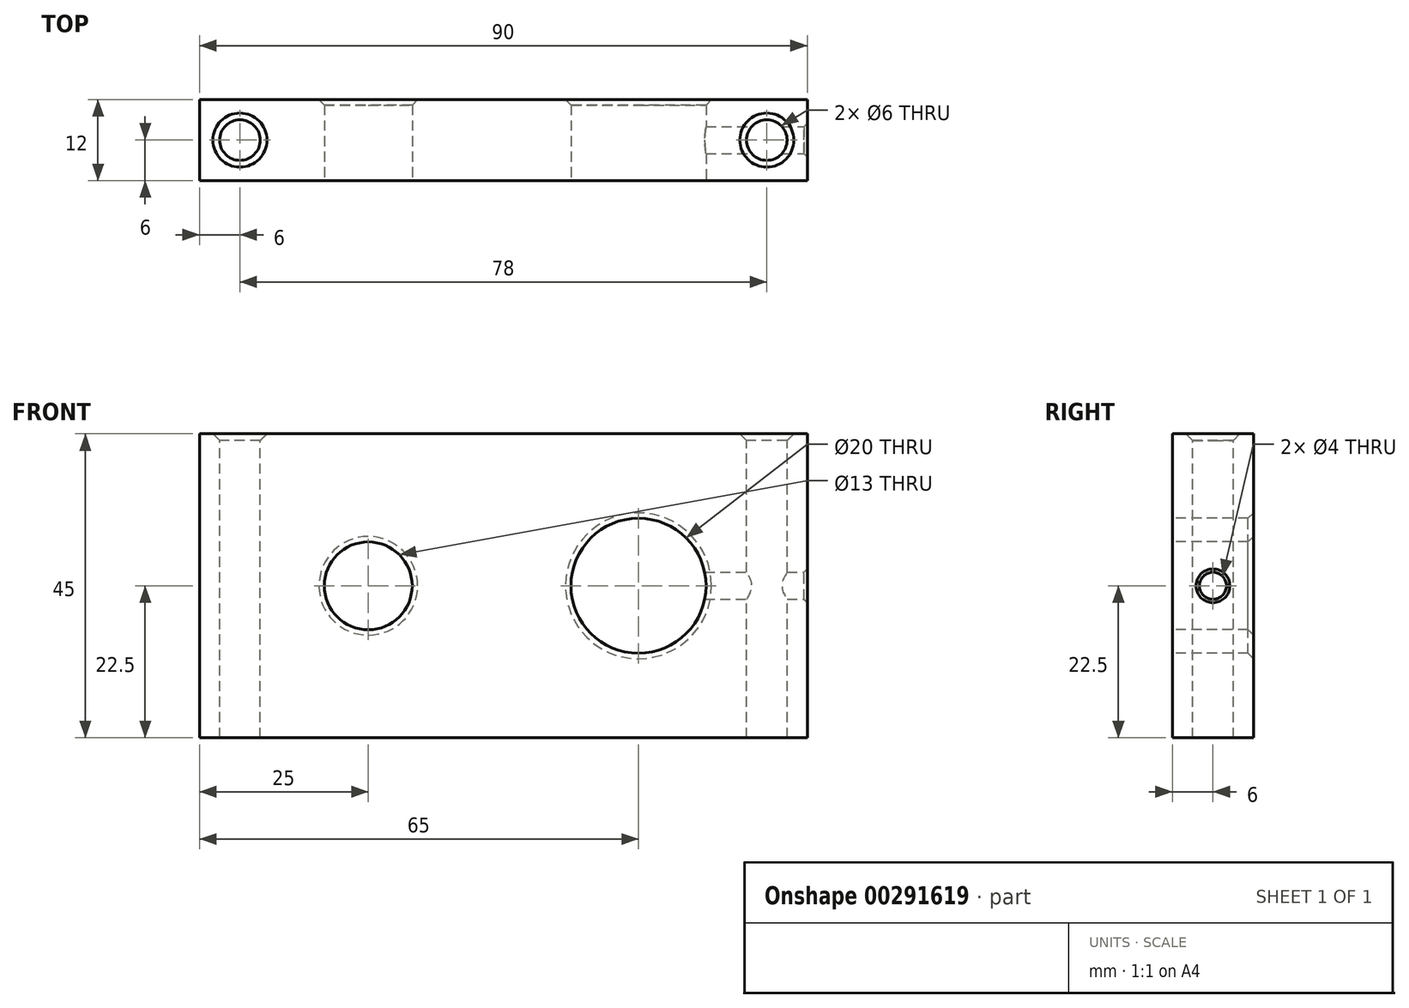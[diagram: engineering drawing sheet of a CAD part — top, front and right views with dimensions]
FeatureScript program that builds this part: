
annotation { "Feature Type Name" : "Feature", "Feature Type Description" : "" }
export const myFeature = defineFeature(function(context is Context, id is Id, definition is map)
    precondition{}
    {
        {
            var Q0;
            Q0=qCreatedBy(makeId("Front.planeOp"),FACE);
            var sketch = newSketch(context, id + "F0", { "sketchPlane" : qUnion([Q0])});
            skLineSegment(sketch, "E0.bottom", {"start": v(-45, 22.5) * mm, "end": v(45, 22.5) * mm});
            skLineSegment(sketch, "E0.top", {"start": v(-45, -22.5) * mm, "end": v(45, -22.5) * mm});
            skLineSegment(sketch, "E0.left", {"start": v(-45, 22.5) * mm, "end": v(-45, -22.5) * mm});
            skLineSegment(sketch, "E0.right", {"start": v(45, 22.5) * mm, "end": v(45, -22.5) * mm});
            skSolve(sketch);
        }
        {
            var Q0;
            Q0=makeQuery(id+"F0.imprint","IMPRINT",FACE,{"disambiguationData":[TD([[makeQuery(id+"F0.imprint","IMPRINT",EDGE,{"derivedFrom":sQuery(id+"F0.wireOp",EDGE,"E0.bottom")}),-1.0]])]});
            extrude(context, id + "F1", {"entities" : qUnion([Q0]), "oppositeDirection" : true, "depth" : 12 * mm});
        }
        {
            var Q0;
            Q0=qCreatedBy(makeId("Front.planeOp"),FACE);
            var sketch = newSketch(context, id + "F2", { "sketchPlane" : qUnion([Q0])});
            skCircle(sketch, "E1", {"center": v(-20, 0) * mm, "radius": 6.5 * mm});
            skCircle(sketch, "E2", {"center": v(20, 0) * mm, "radius": 10 * mm});
            skSolve(sketch);
        }
        {
            var Q0;
            Q0 = qSketchRegion(id + "F2", true);
            extrude(context, id + "F3", {"entities" : qUnion([Q0]), "operationType" : NewBodyOperationType.REMOVE, "oppositeDirection" : true, "depth" : 25 * mm});
        }
        {
            var Q0;
            Q0=makeQuery(id+"F3.boolean.opBoolean","COPY",EDGE,{"derivedFrom":makeQuery(id+"F3.opExtrude","CAP_EDGE",EDGE,{"disambiguationData":[OSD([sQuery(id+"F2.wireOp",EDGE,"E1")])],"isStart":true})});
            var Q1;
            Q1=makeQuery(id+"F3.boolean.opBoolean","INTERSECT",EDGE,{"derivedFrom":[makeQuery(id+"F1.opExtrude","CAP_FACE",FACE,{"disambiguationData":[OSD([sQuery(id+"F0.wireOp",EDGE,"E0.bottom"),sQuery(id+"F0.wireOp",EDGE,"E0.top"),sQuery(id+"F0.wireOp",EDGE,"E0.left"),sQuery(id+"F0.wireOp",EDGE,"E0.right")])],"isStart":false}),makeQuery(id+"F3.opExtrude","SWEPT_FACE",FACE,{"disambiguationData":[OSD([sQuery(id+"F2.wireOp",EDGE,"E1")])]})]});
            var Q2;
            Q2=makeQuery(id+"F3.boolean.opBoolean","COPY",EDGE,{"derivedFrom":makeQuery(id+"F3.opExtrude","CAP_EDGE",EDGE,{"disambiguationData":[OSD([sQuery(id+"F2.wireOp",EDGE,"E2")])],"isStart":true})});
            var Q3;
            Q3=makeQuery(id+"F3.boolean.opBoolean","INTERSECT",EDGE,{"derivedFrom":[makeQuery(id+"F1.opExtrude","CAP_FACE",FACE,{"disambiguationData":[OSD([sQuery(id+"F0.wireOp",EDGE,"E0.bottom"),sQuery(id+"F0.wireOp",EDGE,"E0.top"),sQuery(id+"F0.wireOp",EDGE,"E0.left"),sQuery(id+"F0.wireOp",EDGE,"E0.right")])],"isStart":false}),makeQuery(id+"F3.opExtrude","SWEPT_FACE",FACE,{"disambiguationData":[OSD([sQuery(id+"F2.wireOp",EDGE,"E2")])]})]});
            chamfer(context, id + "F4", {"entities" : qUnion([Q0, Q1, Q2, Q3]), "width" : 0.8 * mm, "tangentPropagation" : true});
        }
        {
            var Q0;
            Q0=makeQuery(id+"F1.opExtrude","SWEPT_FACE",FACE,{"disambiguationData":[OSD([sQuery(id+"F0.wireOp",EDGE,"E0.bottom")])]});
            cPlane(context, id + "F5", {"entities" : qUnion([Q0]), "cplaneType" : CPlaneType.OFFSET, "offset" : 0 * mm, "width" : 150 * mm, "height" : 150 * mm});
        }
        {
            var Q0;
            Q0=qCreatedBy(id+"F5.planeOp",FACE);
            var sketch = newSketch(context, id + "F6", { "sketchPlane" : qUnion([Q0])});
            skPoint(sketch, "E3", {"position": v(-39, 6) * mm});
            skPoint(sketch, "E4", {"position": v(39, 6) * mm});
            skSolve(sketch);
        }
        {
            var Q0;
            Q0=sQuery(id+"F6.wireOp",VERTEX,"E3");
            var Q1;
            Q1=sQuery(id+"F6.wireOp",VERTEX,"E4");
            var Q2;
            Q2=makeQuery(id+"F1.opExtrude","SWEPT_BODY",BODY,{"disambiguationData":[OSD([sQuery(id+"F0.wireOp",EDGE,"E0.bottom"),sQuery(id+"F0.wireOp",EDGE,"E0.top"),sQuery(id+"F0.wireOp",EDGE,"E0.left"),sQuery(id+"F0.wireOp",EDGE,"E0.right")])]});
            hole(context, id + "F7", {"style" : HoleStyle.C_SINK, "endStyle" : HoleEndStyle.THROUGH, "holeDiameter" : 6 * mm, "cSinkDiameter" : 8 * mm, "cSinkAngle" : 90 * degree, "tappedDepth" : 12 * mm, "tapClearance" : 3, "startFromSketch" : true, "locations" : qUnion([Q0, Q1]), "scope" : qUnion([Q2])});
        }
        {
            var Q0;
            Q0=makeQuery(id+"F1.opExtrude","SWEPT_FACE",FACE,{"disambiguationData":[OSD([sQuery(id+"F0.wireOp",EDGE,"E0.right")])]});
            var sketch = newSketch(context, id + "F8", { "sketchPlane" : qUnion([Q0])});
            skCircle(sketch, "E5", {"center": v(6, 0) * mm, "radius": 3 * mm});
            skSolve(sketch);
        }
        {
            var Q0;
            Q0=sQuery(id+"F8.wireOp",VERTEX,"E5.center");
            var Q1;
            Q1=makeQuery(id+"F1.opExtrude","SWEPT_BODY",BODY,{"disambiguationData":[OSD([sQuery(id+"F0.wireOp",EDGE,"E0.bottom"),sQuery(id+"F0.wireOp",EDGE,"E0.top"),sQuery(id+"F0.wireOp",EDGE,"E0.left"),sQuery(id+"F0.wireOp",EDGE,"E0.right")])]});
            hole(context, id + "F9", {"style" : HoleStyle.C_SINK, "endStyle" : HoleEndStyle.BLIND, "holeDiameter" : 4 * mm, "cSinkDiameter" : 5 * mm, "cSinkAngle" : 90 * degree, "holeDepth" : 30 * mm, "tappedDepth" : 12 * mm, "tapClearance" : 3, "startFromSketch" : true, "locations" : qUnion([Q0]), "scope" : qUnion([Q1])});
        }
    });
